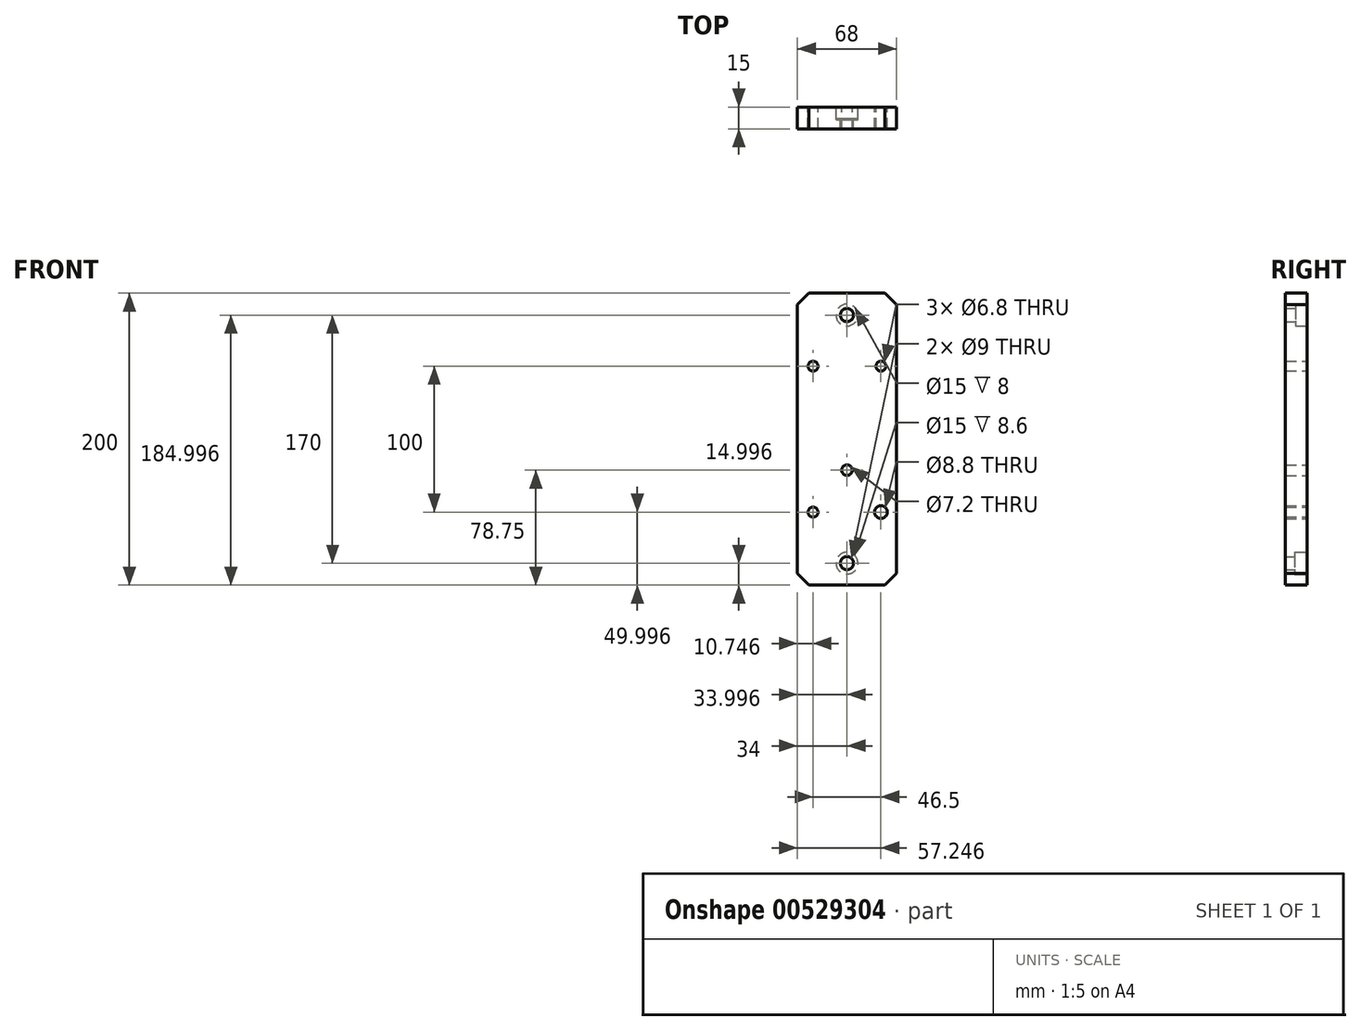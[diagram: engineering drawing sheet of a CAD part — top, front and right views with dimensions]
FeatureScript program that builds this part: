
annotation { "Feature Type Name" : "Feature", "Feature Type Description" : "" }
export const myFeature = defineFeature(function(context is Context, id is Id, definition is map)
    precondition{}
    {
        {
            var Q0;
            Q0=qCreatedBy(makeId("Front.planeOp"),FACE);
            var sketch = newSketch(context, id + "F0", { "sketchPlane" : qUnion([Q0])});
            skLineSegment(sketch, "E0", {"start": v(-26, 121.25) * mm, "end": v(-34, 113.25) * mm});
            skLineSegment(sketch, "E1", {"start": v(26, 121.25) * mm, "end": v(-26, 121.25) * mm});
            skLineSegment(sketch, "E2", {"start": v(34, 113.25) * mm, "end": v(26, 121.25) * mm});
            skLineSegment(sketch, "E3", {"start": v(34, -70.75) * mm, "end": v(34, 113.25) * mm});
            skLineSegment(sketch, "E4", {"start": v(26, -78.75) * mm, "end": v(34, -70.75) * mm});
            skLineSegment(sketch, "E5", {"start": v(-26, -78.75) * mm, "end": v(26, -78.75) * mm});
            skLineSegment(sketch, "E6", {"start": v(-34, -70.75) * mm, "end": v(-26, -78.75) * mm});
            skLineSegment(sketch, "E7", {"start": v(-34, 113.25) * mm, "end": v(-34, -70.75) * mm});
            skCircle(sketch, "E8", {"center": v(-23.25, 71.25) * mm, "radius": 3.4 * mm});
            skCircle(sketch, "E9", {"center": v(23.25, 71.25) * mm, "radius": 3.4 * mm});
            skCircle(sketch, "E10", {"center": v(23.25, -28.75) * mm, "radius": 3.4 * mm});
            skCircle(sketch, "E11", {"center": v(-23.25, -28.75) * mm, "radius": 3.4 * mm});
            skCircle(sketch, "E12", {"center": v(0, -63.75) * mm, "radius": 4.5 * mm});
            skCircle(sketch, "E13", {"center": v(0, 106.25) * mm, "radius": 4.5 * mm});
            skPoint(sketch, "E14", {"position": v(0, 0) * mm});
            skSolve(sketch);
        }
        {
            var Q0;
            Q0 = qSketchRegion(id + "F0", true);
            extrude(context, id + "F1", {"entities" : qUnion([Q0]), "depth" : 15 * mm, "offsetDistance" : 25 * mm});
        }
        {
            var Q0;
            Q0=sQuery(id+"F0.wireOp",VERTEX,"E13.center");
            var Q1;
            Q1=makeQuery(id+"F1.opExtrude","SWEPT_BODY",BODY,{"disambiguationData":[OSD([sQuery(id+"F0.wireOp",EDGE,"E0"),sQuery(id+"F0.wireOp",EDGE,"E1"),sQuery(id+"F0.wireOp",EDGE,"E2"),sQuery(id+"F0.wireOp",EDGE,"E3"),sQuery(id+"F0.wireOp",EDGE,"E4"),sQuery(id+"F0.wireOp",EDGE,"E5"),sQuery(id+"F0.wireOp",EDGE,"E6"),sQuery(id+"F0.wireOp",EDGE,"E7"),sQuery(id+"F0.wireOp",EDGE,"E8"),sQuery(id+"F0.wireOp",EDGE,"E9"),sQuery(id+"F0.wireOp",EDGE,"E10"),sQuery(id+"F0.wireOp",EDGE,"E11"),sQuery(id+"F0.wireOp",EDGE,"E12"),sQuery(id+"F0.wireOp",EDGE,"E13")])]});
            hole(context, id + "F2", {"style" : HoleStyle.C_BORE, "endStyle" : HoleEndStyle.THROUGH, "oppositeDirection" : true, "holeDiameter" : 8.8 * mm, "cBoreDiameter" : 15 * mm, "cBoreDepth" : 8 * mm, "isTappedThrough" : true, "tappedDepth" : 12 * mm, "tapClearance" : 3, "locations" : qUnion([Q0]), "scope" : qUnion([Q1])});
        }
        {
            var Q0;
            Q0=sQuery(id+"F0.wireOp",VERTEX,"E12.center");
            var Q1;
            Q1=makeQuery(id+"F1.opExtrude","SWEPT_BODY",BODY,{"disambiguationData":[OSD([sQuery(id+"F0.wireOp",EDGE,"E0"),sQuery(id+"F0.wireOp",EDGE,"E1"),sQuery(id+"F0.wireOp",EDGE,"E2"),sQuery(id+"F0.wireOp",EDGE,"E3"),sQuery(id+"F0.wireOp",EDGE,"E4"),sQuery(id+"F0.wireOp",EDGE,"E5"),sQuery(id+"F0.wireOp",EDGE,"E6"),sQuery(id+"F0.wireOp",EDGE,"E7"),sQuery(id+"F0.wireOp",EDGE,"E8"),sQuery(id+"F0.wireOp",EDGE,"E9"),sQuery(id+"F0.wireOp",EDGE,"E10"),sQuery(id+"F0.wireOp",EDGE,"E11"),sQuery(id+"F0.wireOp",EDGE,"E12"),sQuery(id+"F0.wireOp",EDGE,"E13")])]});
            hole(context, id + "F3", {"style" : HoleStyle.C_BORE, "endStyle" : HoleEndStyle.THROUGH, "oppositeDirection" : true, "holeDiameter" : 8.8 * mm, "cBoreDiameter" : 15 * mm, "cBoreDepth" : 8.6 * mm, "isTappedThrough" : true, "tappedDepth" : 12 * mm, "tapClearance" : 3, "locations" : qUnion([Q0]), "scope" : qUnion([Q1])});
        }
        {
            var Q0;
            Q0=sQuery(id+"F0.wireOp",VERTEX,"E10.center");
            var Q1;
            Q1=makeQuery(id+"F1.opExtrude","SWEPT_BODY",BODY,{"disambiguationData":[OSD([sQuery(id+"F0.wireOp",EDGE,"E0"),sQuery(id+"F0.wireOp",EDGE,"E1"),sQuery(id+"F0.wireOp",EDGE,"E2"),sQuery(id+"F0.wireOp",EDGE,"E3"),sQuery(id+"F0.wireOp",EDGE,"E4"),sQuery(id+"F0.wireOp",EDGE,"E5"),sQuery(id+"F0.wireOp",EDGE,"E6"),sQuery(id+"F0.wireOp",EDGE,"E7"),sQuery(id+"F0.wireOp",EDGE,"E8"),sQuery(id+"F0.wireOp",EDGE,"E9"),sQuery(id+"F0.wireOp",EDGE,"E10"),sQuery(id+"F0.wireOp",EDGE,"E11"),sQuery(id+"F0.wireOp",EDGE,"E12"),sQuery(id+"F0.wireOp",EDGE,"E13")])]});
            hole(context, id + "F4", {"style" : HoleStyle.SIMPLE, "endStyle" : HoleEndStyle.THROUGH, "oppositeDirection" : true, "standardTappedOrClearance" : lookupTablePath({ "standard" : "ISO", "engagement" : "75%", "pitch" : "1.25 mm", "size" : "M10", "type" : "Tapped" }), "standardBlindInLast" : lookupTablePath({ "standard" : "ISO", "engagement" : "75%", "pitch" : "1.25 mm", "size" : "M10", "type" : "Tapped" }), "holeDiameter" : 8.8 * mm, "showTappedDepth" : true, "tappedDepth" : 16.25 * mm, "tapClearance" : 3, "locations" : qUnion([Q0]), "scope" : qUnion([Q1]), "majorDiameter" : 10 * mm});
        }
        {
            var Q0;
            Q0=sQuery(id+"F0.wireOp",VERTEX,"E14");
            var Q1;
            Q1=makeQuery(id+"F1.opExtrude","SWEPT_BODY",BODY,{"disambiguationData":[OSD([sQuery(id+"F0.wireOp",EDGE,"E0"),sQuery(id+"F0.wireOp",EDGE,"E1"),sQuery(id+"F0.wireOp",EDGE,"E2"),sQuery(id+"F0.wireOp",EDGE,"E3"),sQuery(id+"F0.wireOp",EDGE,"E4"),sQuery(id+"F0.wireOp",EDGE,"E5"),sQuery(id+"F0.wireOp",EDGE,"E6"),sQuery(id+"F0.wireOp",EDGE,"E7"),sQuery(id+"F0.wireOp",EDGE,"E8"),sQuery(id+"F0.wireOp",EDGE,"E9"),sQuery(id+"F0.wireOp",EDGE,"E10"),sQuery(id+"F0.wireOp",EDGE,"E11"),sQuery(id+"F0.wireOp",EDGE,"E12"),sQuery(id+"F0.wireOp",EDGE,"E13")])]});
            hole(context, id + "F5", {"style" : HoleStyle.SIMPLE, "endStyle" : HoleEndStyle.THROUGH, "oppositeDirection" : true, "standardTappedOrClearance" : lookupTablePath({ "standard" : "ISO", "engagement" : "50%", "pitch" : "1.25 mm", "size" : "M8", "type" : "Tapped" }), "standardBlindInLast" : lookupTablePath({ "standard" : "ISO", "engagement" : "50%", "pitch" : "1.25 mm", "size" : "M8", "type" : "Tapped" }), "holeDiameter" : 7.2 * mm, "showTappedDepth" : true, "tappedDepth" : 16.25 * mm, "tapClearance" : 3, "locations" : qUnion([Q0]), "scope" : qUnion([Q1]), "majorDiameter" : 8 * mm});
        }
    });
